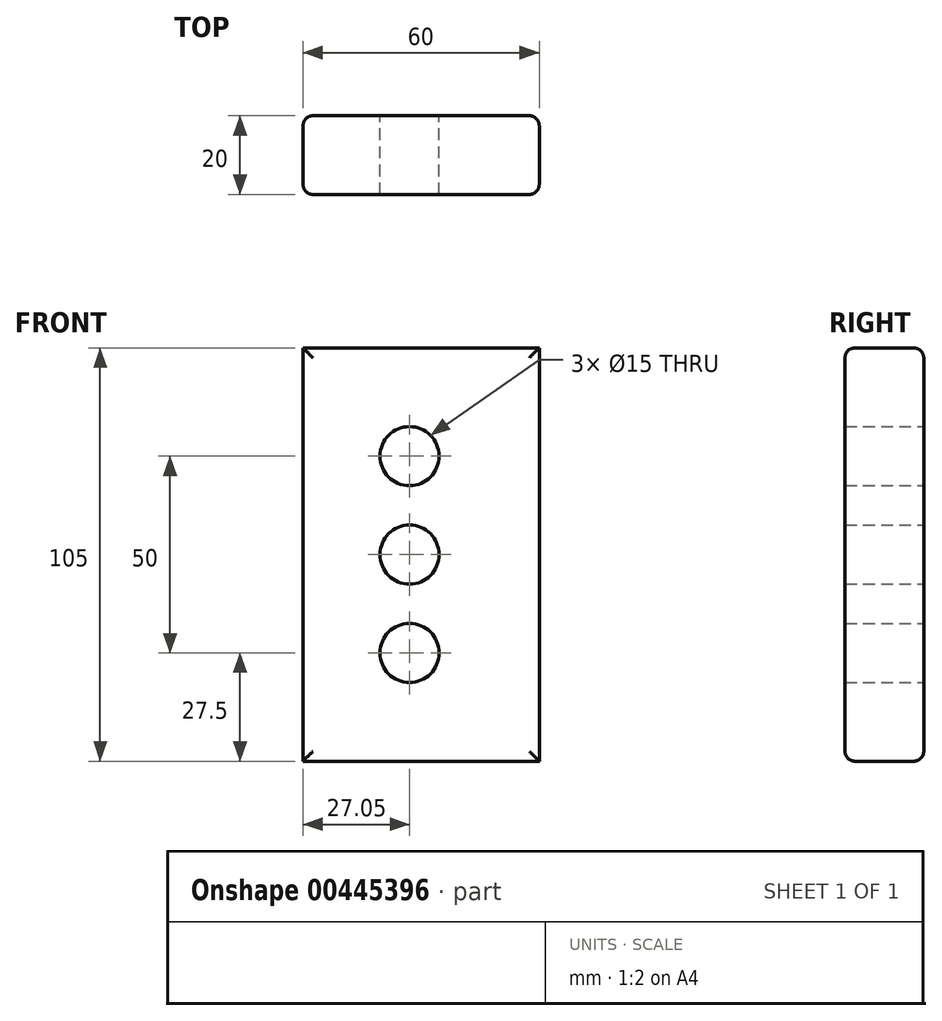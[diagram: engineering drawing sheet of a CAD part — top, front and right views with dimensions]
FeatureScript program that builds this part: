
annotation { "Feature Type Name" : "Feature", "Feature Type Description" : "" }
export const myFeature = defineFeature(function(context is Context, id is Id, definition is map)
    precondition{}
    {
        {
            var Q0;
            Q0=qCreatedBy(makeId("Front.planeOp"),FACE);
            var sketch = newSketch(context, id + "F0", { "sketchPlane" : qUnion([Q0])});
            skLineSegment(sketch, "E0.bottom", {"start": v(-27.05, 77.5) * mm, "end": v(32.95, 77.5) * mm});
            skLineSegment(sketch, "E0.top", {"start": v(-27.05, -27.5) * mm, "end": v(32.95, -27.5) * mm});
            skLineSegment(sketch, "E0.left", {"start": v(-27.05, 77.5) * mm, "end": v(-27.05, -27.5) * mm});
            skLineSegment(sketch, "E0.right", {"start": v(32.95, 77.5) * mm, "end": v(32.95, -27.5) * mm});
            skCircle(sketch, "E1", {"center": v(0, 25) * mm, "radius": 7.5 * mm});
            skCircle(sketch, "E2", {"center": v(0, 0) * mm, "radius": 7.5 * mm});
            skCircle(sketch, "E3", {"center": v(0, 50) * mm, "radius": 7.5 * mm});
            skSolve(sketch);
        }
        {
            var Q0;
            Q0=makeQuery(id+"F0.imprint","IMPRINT",FACE,{"disambiguationData":[TD([[makeQuery(id+"F0.imprint","IMPRINT",EDGE,{"derivedFrom":sQuery(id+"F0.wireOp",EDGE,"E0.bottom")}),-1.0]])]});
            extrude(context, id + "F1", {"entities" : qUnion([Q0]), "depth" : 20 * mm});
        }
        {
            var Q0;
            Q0=makeQuery(id+"F1.opExtrude","CAP_EDGE",EDGE,{"disambiguationData":[OSD([sQuery(id+"F0.wireOp",EDGE,"E0.left")])],"isStart":false});
            var Q1;
            Q1=makeQuery(id+"F1.opExtrude","CAP_EDGE",EDGE,{"disambiguationData":[OSD([sQuery(id+"F0.wireOp",EDGE,"E0.top")])],"isStart":false});
            var Q2;
            Q2=makeQuery(id+"F1.opExtrude","CAP_EDGE",EDGE,{"disambiguationData":[OSD([sQuery(id+"F0.wireOp",EDGE,"E0.right")])],"isStart":false});
            var Q3;
            Q3=makeQuery(id+"F1.opExtrude","CAP_EDGE",EDGE,{"disambiguationData":[OSD([sQuery(id+"F0.wireOp",EDGE,"E0.bottom")])],"isStart":false});
            fillet(context, id + "F2", {"entities" : qUnion([Q0, Q1, Q2, Q3]), "radius" : 2.5 * mm, "tangentPropagation" : true, "allowEdgeOverflow" : false});
        }
        {
            var Q0;
            Q0=makeQuery(id+"F1.opExtrude","CAP_EDGE",EDGE,{"disambiguationData":[OSD([sQuery(id+"F0.wireOp",EDGE,"E0.right")])],"isStart":true});
            var Q1;
            Q1=makeQuery(id+"F1.opExtrude","CAP_EDGE",EDGE,{"disambiguationData":[OSD([sQuery(id+"F0.wireOp",EDGE,"E0.top")])],"isStart":true});
            var Q2;
            Q2=makeQuery(id+"F1.opExtrude","CAP_EDGE",EDGE,{"disambiguationData":[OSD([sQuery(id+"F0.wireOp",EDGE,"E0.left")])],"isStart":true});
            var Q3;
            Q3=makeQuery(id+"F1.opExtrude","CAP_EDGE",EDGE,{"disambiguationData":[OSD([sQuery(id+"F0.wireOp",EDGE,"E0.bottom")])],"isStart":true});
            fillet(context, id + "F3", {"entities" : qUnion([Q0, Q1, Q2, Q3]), "radius" : 2.5 * mm, "tangentPropagation" : true, "allowEdgeOverflow" : false});
        }
    });
